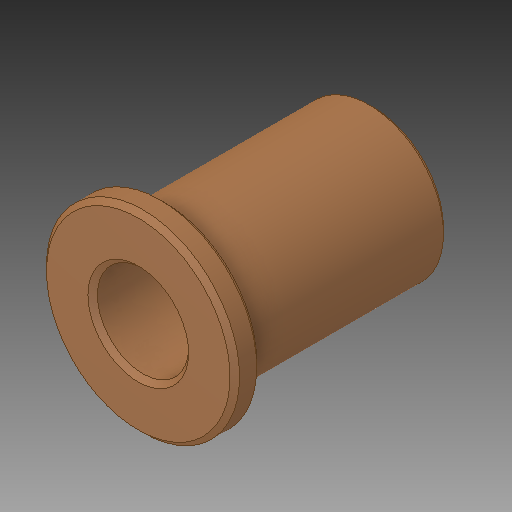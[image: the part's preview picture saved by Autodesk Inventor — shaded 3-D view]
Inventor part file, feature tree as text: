
AUTODESK INVENTOR PART (.ipt)
format: ipt  version: 2018 (Build 220112000, 112)  size: 152,576 bytes
history: native  units: in
note: dims shown in document units (in); Inventor stores cm internally (conversion verified against a paired STEP export)
features: chamfer x1
ambient origin geometry x8: Origin, YZ Plane, XZ Plane, XY Plane, X Axis, Y Axis, Z Axis, Center Point
bodies: Solid1 (feature_tree)
feature tree (1):
  chamfer  "Chamfer1"  [1 undecoded]
note: 1 required parameter value undecoded (feature->parameter linkage not recoverable at this tier; creation-order binding heuristic only, values carry confidence <= 0.55)
